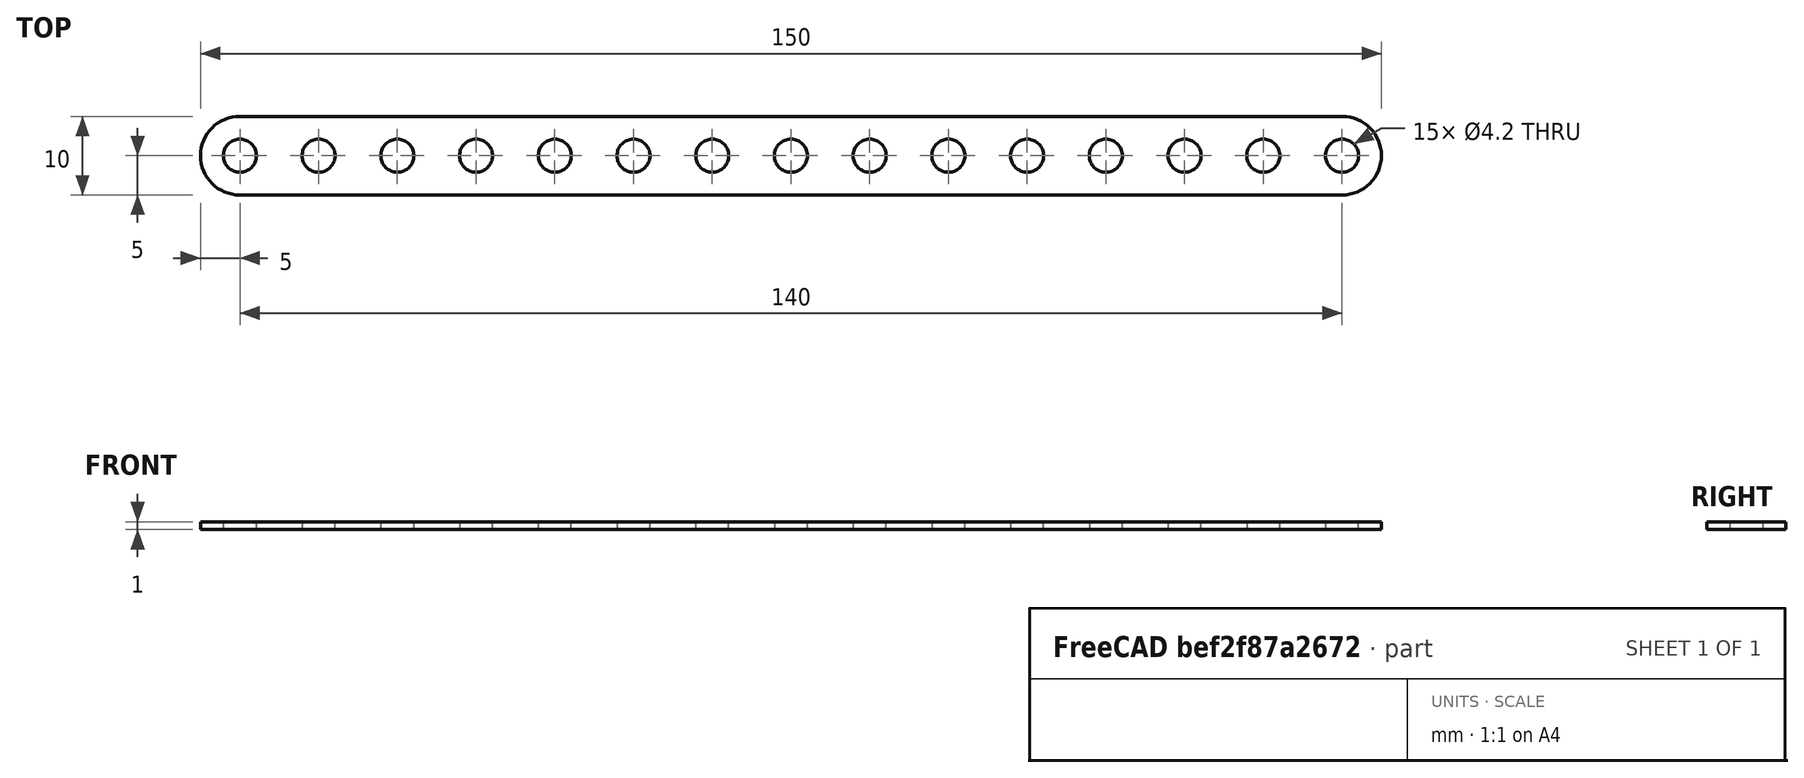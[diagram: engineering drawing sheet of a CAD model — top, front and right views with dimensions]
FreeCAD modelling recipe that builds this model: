
FCSTD DOCUMENT  (FreeCAD 0.16RUnknown)
Label: strip_1x15
License: All rights reserved
LicenseURL: http://en.wikipedia.org/wiki/All_rights_reserved
objects: Sketcher::SketchObject×1, PartDesign::Pad×1, Drawing::FeatureViewPart×1, Drawing::FeaturePage×1
note: 3 computed .brp shape members not serialized (recipe doc carries the construction recipe); baked Part::Feature solids carry a one-line shape summary decoded from their .brp

FEATURE [Sketcher::SketchObject] Sketch
  sketch-geometry (33):
    g0: Circle CenterX=0 CenterY=0 CenterZ=0 NormalX=0 NormalY=0 NormalZ=1 Radius=2.1
    g1: ArcOfCircle CenterX=0 CenterY=0 CenterZ=0 NormalX=0 NormalY=0 NormalZ=1 Radius=5 StartAngle=1.5708 EndAngle=4.71239
    g2: LineSegment StartX=-1.8e-11 StartY=-5 StartZ=0 EndX=140 EndY=-5 EndZ=0
    g3: LineSegment StartX=-1.8e-11 StartY=5 StartZ=0 EndX=140 EndY=5 EndZ=0
    g4: Circle CenterX=10 CenterY=0 CenterZ=0 NormalX=0 NormalY=0 NormalZ=1 Radius=2.1
    g5: LineSegment [constr] StartX=0 StartY=0 StartZ=0 EndX=10 EndY=0 EndZ=0
    g6: Circle CenterX=20 CenterY=0 CenterZ=0 NormalX=0 NormalY=0 NormalZ=1 Radius=2.1
    g7: LineSegment [constr] StartX=10 StartY=0 StartZ=0 EndX=20 EndY=0 EndZ=0
    g8: Circle CenterX=30 CenterY=0 CenterZ=0 NormalX=0 NormalY=0 NormalZ=1 Radius=2.1
    g9: LineSegment [constr] StartX=20 StartY=0 StartZ=0 EndX=30 EndY=0 EndZ=0
    g10: Circle CenterX=40 CenterY=0 CenterZ=0 NormalX=0 NormalY=0 NormalZ=1 Radius=2.1
    g11: LineSegment [constr] StartX=30 StartY=0 StartZ=0 EndX=40 EndY=0 EndZ=0
    g12: Circle CenterX=50 CenterY=0 CenterZ=0 NormalX=0 NormalY=0 NormalZ=1 Radius=2.1
    g13: LineSegment [constr] StartX=40 StartY=0 StartZ=0 EndX=50 EndY=0 EndZ=0
    g14: Circle CenterX=60 CenterY=0 CenterZ=0 NormalX=0 NormalY=0 NormalZ=1 Radius=2.1
    g15: LineSegment [constr] StartX=50 StartY=0 StartZ=0 EndX=60 EndY=0 EndZ=0
    g16: Circle CenterX=70 CenterY=0 CenterZ=0 NormalX=0 NormalY=0 NormalZ=1 Radius=2.1
    g17: LineSegment [constr] StartX=60 StartY=0 StartZ=0 EndX=70 EndY=0 EndZ=0
    g18: Circle CenterX=80 CenterY=0 CenterZ=0 NormalX=0 NormalY=0 NormalZ=1 Radius=2.1
    g19: LineSegment [constr] StartX=70 StartY=0 StartZ=0 EndX=80 EndY=0 EndZ=0
    g20: Circle CenterX=90 CenterY=0 CenterZ=0 NormalX=0 NormalY=0 NormalZ=1 Radius=2.1
    g21: LineSegment [constr] StartX=80 StartY=0 StartZ=0 EndX=90 EndY=0 EndZ=0
    g22: Circle CenterX=100 CenterY=0 CenterZ=0 NormalX=0 NormalY=0 NormalZ=1 Radius=2.1
    g23: LineSegment [constr] StartX=90 StartY=0 StartZ=0 EndX=100 EndY=0 EndZ=0
    g24: Circle CenterX=110 CenterY=0 CenterZ=0 NormalX=0 NormalY=0 NormalZ=1 Radius=2.1
    g25: LineSegment [constr] StartX=100 StartY=0 StartZ=0 EndX=110 EndY=0 EndZ=0
    g26: Circle CenterX=120 CenterY=0 CenterZ=0 NormalX=0 NormalY=0 NormalZ=1 Radius=2.1
    g27: LineSegment [constr] StartX=110 StartY=0 StartZ=0 EndX=120 EndY=0 EndZ=0
    g28: Circle CenterX=130 CenterY=0 CenterZ=0 NormalX=0 NormalY=0 NormalZ=1 Radius=2.1
    g29: LineSegment [constr] StartX=120 StartY=0 StartZ=0 EndX=130 EndY=0 EndZ=0
    g30: Circle CenterX=140 CenterY=0 CenterZ=0 NormalX=0 NormalY=0 NormalZ=1 Radius=2.1
    g31: LineSegment [constr] StartX=130 StartY=0 StartZ=0 EndX=140 EndY=0 EndZ=0
    g32: ArcOfCircle CenterX=140 CenterY=0 CenterZ=0 NormalX=0 NormalY=0 NormalZ=1 Radius=5 StartAngle=4.71239 EndAngle=7.85398
  constraints (84):
    c: Radius(g0) = 2.1
    c: Angle(g0,g-1) = 0
    c: Tangent(g1,g3) = 1.5708
    c: Tangent(g1,g2) = -1.5708
    c: Horizontal(g2)
    c: Radius(g1) = 5
    c: Equal(g0,g4) = 2.1
    c: Coincident(g0,g5)
    c: Coincident(g4,g5)
    c: Distance(g5) = 10
    c: Angle(g5) = 0
    c: Equal(g0,g6) = 2.1
    c: Coincident(g4,g7)
    c: Coincident(g6,g7)
    c: Equal(g5,g7)
    c: Parallel(g7,g5)
    c: Equal(g0,g8) = 2.1
    c: Coincident(g6,g9)
    c: Coincident(g8,g9)
    c: Equal(g5,g9)
    c: Parallel(g9,g5)
    c: Equal(g0,g10) = 2.1
    c: Coincident(g8,g11)
    c: Coincident(g10,g11)
    c: Equal(g5,g11)
    c: Parallel(g11,g5)
    c: Equal(g0,g12) = 2.1
    c: Coincident(g10,g13)
    c: Coincident(g12,g13)
    c: Equal(g5,g13)
    c: Parallel(g13,g5)
    c: Equal(g0,g14) = 2.1
    c: Coincident(g12,g15)
    c: Coincident(g14,g15)
    c: Equal(g5,g15)
    c: Parallel(g15,g5)
    c: Equal(g0,g16) = 2.1
    c: Coincident(g14,g17)
    c: Coincident(g16,g17)
    c: Equal(g5,g17)
    c: Parallel(g17,g5)
    c: Equal(g0,g18) = 2.1
    c: Coincident(g16,g19)
    c: Coincident(g18,g19)
    c: Equal(g5,g19)
    c: Parallel(g19,g5)
    c: Equal(g0,g20) = 2.1
    c: Coincident(g18,g21)
    c: Coincident(g20,g21)
    c: Equal(g5,g21)
    c: Parallel(g21,g5)
    c: Equal(g0,g22) = 2.1
    c: Coincident(g20,g23)
    c: Coincident(g22,g23)
    c: Equal(g5,g23)
    c: Parallel(g23,g5)
    c: Equal(g0,g24) = 2.1
    c: Coincident(g22,g25)
    c: Coincident(g24,g25)
    c: Equal(g5,g25)
    c: Parallel(g25,g5)
    c: Equal(g0,g26) = 2.1
    c: Coincident(g24,g27)
    c: Coincident(g26,g27)
    c: Equal(g5,g27)
    c: Parallel(g27,g5)
    c: Equal(g0,g28) = 2.1
    c: Coincident(g26,g29)
    c: Coincident(g28,g29)
    c: Equal(g5,g29)
    c: Parallel(g29,g5)
    c: Equal(g0,g30) = 2.1
    c: Coincident(g28,g31)
    c: Coincident(g30,g31)
    c: Equal(g5,g31)
    c: Parallel(g31,g5)
    c: Coincident(g0,g-1)
    c: Symmetric(g3,g2,g-1)
    c: Horizontal(g3)
    c: Coincident(g32,g30)
    c: Coincident(g32,g3)
    c: Coincident(g32,g2)
    c: Angle(g32) = 3.14159
    c: Coincident(g1,g-1)
FEATURE [PartDesign::Pad] Pad
  Length = 1
  Length2 = 100
  Sketch = -> Sketch
  Type = 0
FEATURE [Drawing::FeatureViewPart] Ortho002  label="Ortho_0_1"
  Direction = (0,0,1)
  HiddenWidth = 0.15
  LineWidth = 0.35
  Rotation = 90
  ShowHiddenLines = false
  ShowSmoothLines = false
  Source = -> Pad
  Tolerance = 0.05
  ViewResult = <g id="Ortho_0_1"\n   transform="rotate(90,105,66) translate(105,66) scale(1,1)"\n  >\n<g   stroke="rgb(0, 0, 0)"\n   stroke-width="0.35"\n   stroke-linecap="butt"\n   stroke-linejoin="miter"\n   fill="none"\n   transform="scale(1,-1)"\n  >\n<path d="M5.33213e-13 5 A5 5 0 1 1 5.00902e-13 -5" /><path id= "2" d=" M -1.77906e-11 -5 L 140 -5 " />\n<path d="M140 -5 A5 5 0 0 1 140 5" /><path id= "4" d=" M -1.77912e-11 5 L 140 5 " />\n<circle cx ="10" cy ="-7.95841e-18" r ="2.1" /><circle cx ="0" cy ="0" r ="2.1" /><circle cx ="140" cy ="-1.11418e-16" r ="2.1" /><circle cx ="130" cy ="-1.03459e-16" r ="2.1" /><circle cx ="120" cy ="-9.55009e-17" r ="2.1" /><circle cx ="110" cy ="-8.75425e-17" r ="2.1" /><circle cx ="100" cy ="-7.95841e-17" r ="2.1" /><circle cx ="90" cy ="-7.16257e-17" r ="2.1" /><circle cx ="80" cy ="-6.36673e-17" r ="2.1" /><circle cx ="70" cy ="-5.57089e-17" r ="2.1" /><circle cx ="60" cy ="-4.77504e-17" r ="2.1" /><circle cx ="50" cy ="-3.9792e-17" r ="2.1" /><circle cx ="40" cy ="-3.18336e-17" r ="2.1" /><circle cx ="30" cy ="-2.38752e-17" r ="2.1" /><circle cx ="20" cy ="-1.59168e-17" r ="2.1" /></g>\n</g>
  Visible = true
  X = 105
  Y = 66
FEATURE [Drawing::FeaturePage] Page
  Group = -> [Ortho002]
